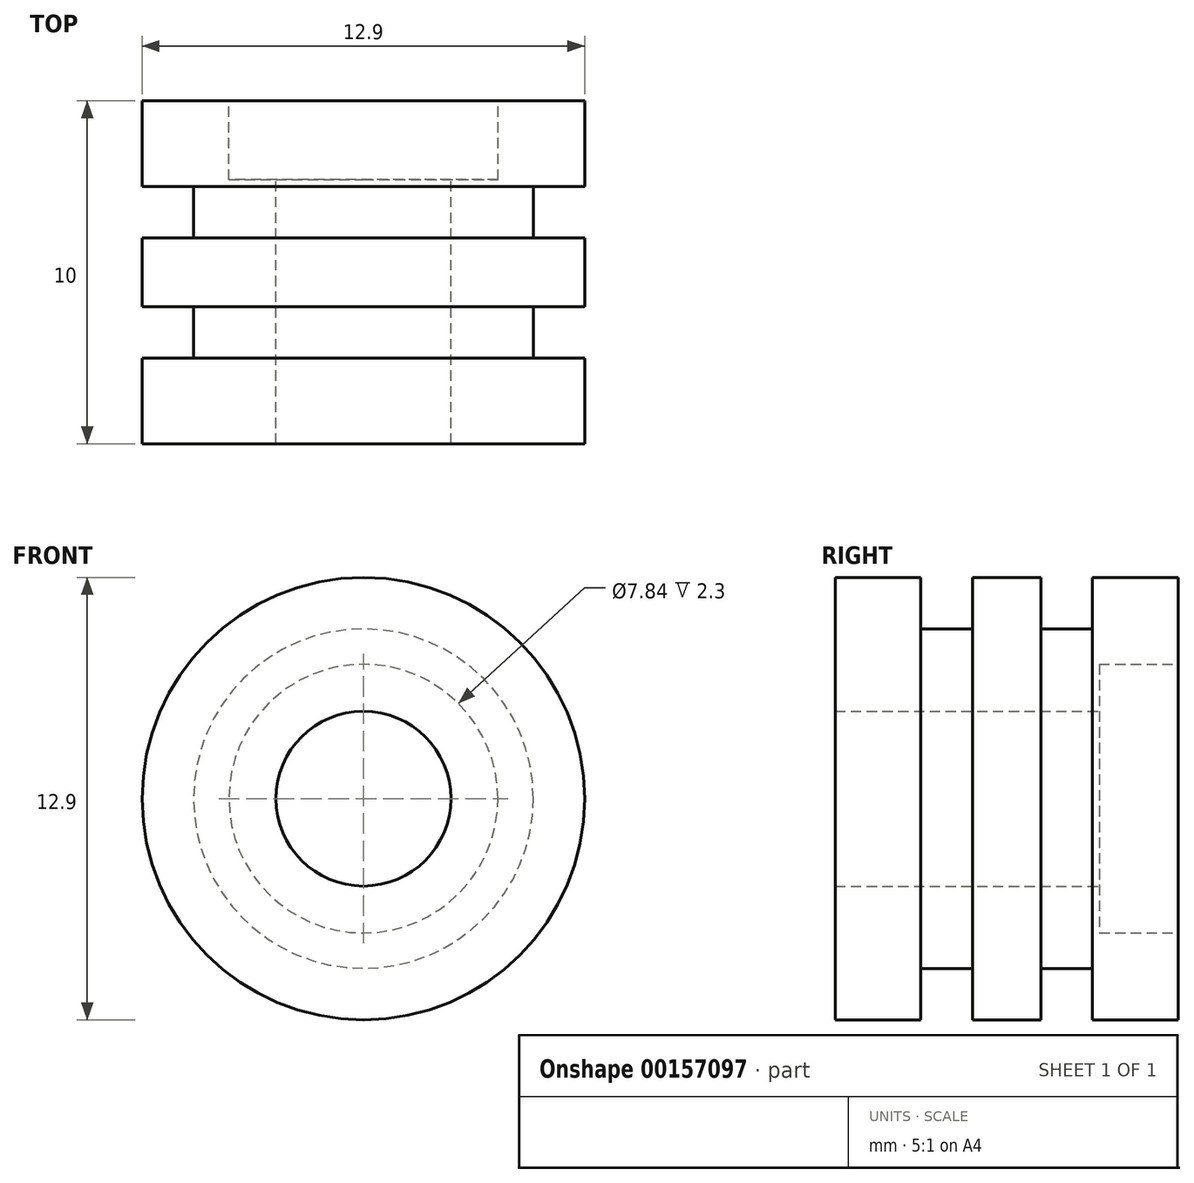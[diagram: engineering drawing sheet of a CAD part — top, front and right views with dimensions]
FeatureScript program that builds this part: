
annotation { "Feature Type Name" : "Feature", "Feature Type Description" : "" }
export const myFeature = defineFeature(function(context is Context, id is Id, definition is map)
    precondition{}
    {
        {
            var Q0;
            Q0=qCreatedBy(makeId("Right.planeOp"),FACE);
            var sketch = newSketch(context, id + "F0", { "sketchPlane" : qUnion([Q0])});
            skLineSegment(sketch, "E0", {"start": v(11.47, 0) * mm, "end": v(0, 0) * mm, "construction": true});
            skLineSegment(sketch, "E1", {"start": v(7.7, 2.55) * mm, "end": v(0, 2.55) * mm});
            skLineSegment(sketch, "E2", {"start": v(7.7, 2.55) * mm, "end": v(7.7, 3.92) * mm});
            skLineSegment(sketch, "E3", {"start": v(10, 3.92) * mm, "end": v(7.7, 3.92) * mm});
            skLineSegment(sketch, "E4", {"start": v(10, 3.92) * mm, "end": v(10, 6.45) * mm});
            skLineSegment(sketch, "E5", {"start": v(7.5, 6.45) * mm, "end": v(10, 6.45) * mm});
            skLineSegment(sketch, "E6", {"start": v(7.5, 6.45) * mm, "end": v(7.5, 4.95) * mm});
            skLineSegment(sketch, "E7", {"start": v(6, 4.95) * mm, "end": v(7.5, 4.95) * mm});
            skLineSegment(sketch, "E8", {"start": v(2.5, 4.95) * mm, "end": v(2.5, 6.45) * mm});
            skLineSegment(sketch, "E9", {"start": v(0, 6.45) * mm, "end": v(2.5, 6.45) * mm});
            skLineSegment(sketch, "E10", {"start": v(0, 6.45) * mm, "end": v(0, 2.55) * mm});
            skLineSegment(sketch, "E11", {"start": v(4, 4.95) * mm, "end": v(4, 6.45) * mm});
            skLineSegment(sketch, "E12", {"start": v(4, 6.45) * mm, "end": v(6, 6.45) * mm});
            skLineSegment(sketch, "E13", {"start": v(6, 6.45) * mm, "end": v(6, 4.95) * mm});
            skLineSegment(sketch, "E14.trimOffspring", {"start": v(4, 4.95) * mm, "end": v(2.5, 4.95) * mm});
            skSolve(sketch);
        }
        {
            var Q0;
            Q0=makeQuery(id+"F0.imprint","IMPRINT",FACE,{"disambiguationData":[TD([[makeQuery(id+"F0.imprint","IMPRINT",EDGE,{"derivedFrom":sQuery(id+"F0.wireOp",EDGE,"E1")}),-1.0]])]});
            var Q1;
            Q1=sQuery(id+"F0.wireOp",EDGE,"E0");
            revolve(context, id + "F1", {"entities" : qUnion([Q0]), "axis" : qUnion([Q1]), "revolveType" : RevolveType.FULL});
        }
    });
